# Revit family: Haworth_Janus_Accessories_Pillows_Rectangle
name_source: partatom
category: Furniture
revit_build: Autodesk Revit 2018 (Build: 20170223_1515(x64)
units: mm (PartAtom-declared; Revit-internal decimal feet)

## family parameters
Always vertical = Yes
Cut with Voids When Loaded = No
OmniClass Number = 23.40.20.00
OmniClass Title = General Furniture and Specialties
Room Calculation Point = No
Shared = No
Work Plane-Based = No

## types (9) — shared parameters
Actual Depth = 5"
Assembly Code = E2020200
Manufacturer = Haworth
Size = Verify Final Dim. w/ Haworth
Sustainability Info = https://www.haworth.com
URL = http://www.haworth.com
URL - Product = https://www.haworth.com
Version = 2
Warranty = http://www.haworth.com

## per-type parameters (varying)
| type | Actual Height | Actual Width | Description | HeightCore | WidthCore |
| HCJC-JP-P2412 | 12" | 24" | Haworth - Janus - Pillows - Rectangle - 24 x 12 | 15/16" | 12 15/16" |
| HCJC-JP-P2014 | 14" | 20" | Haworth - Janus - Pillows - Rectangle - 20 x 14 | 2 15/16" | 8 15/16" |
| HCJC-JP-P2017 | 17" | 20" | Haworth - Janus - Pillows - Rectangle - 20 x 17 | 5 15/16" | 8 15/16" |
| HCJC-JP-P2018 | 18" | 20" | Haworth - Janus - Pillows - Rectangle - 20 x 18 | 6 15/16" | 8 15/16" |
| HCJC-JP-P1812 | 12" | 18" | Haworth - Janus - Pillows - Rectangle - 18 x 12 | 15/16" | 6 15/16" |
| HCJC-JP-P2417 | 17" | 24" | Haworth - Janus - Pillows - Rectangle - 24 x 17 | 5 15/16" | 12 15/16" |
| HCJC-JP-P2815 | 15" | 28" | Haworth - Janus - Pillows - Rectangle - 28 x 15 | 3 15/16" | 16 15/16" |
| HCJC-JP-P2822 | 22" | 28" | Haworth - Janus - Pillows - Rectangle - 28 x 22 | 10 15/16" | 16 15/16" |
| HCJC-JP-P2824 | 24" | 28" | Haworth - Janus - Pillows - Rectangle - 28 x 24 | 12 15/16" | 16 15/16" |

note: column(s) folded — value = type name in every type: Model

## geometry (parser evidence)
native form markers: Sweep x3
no freeform markers — native parametric forms only
